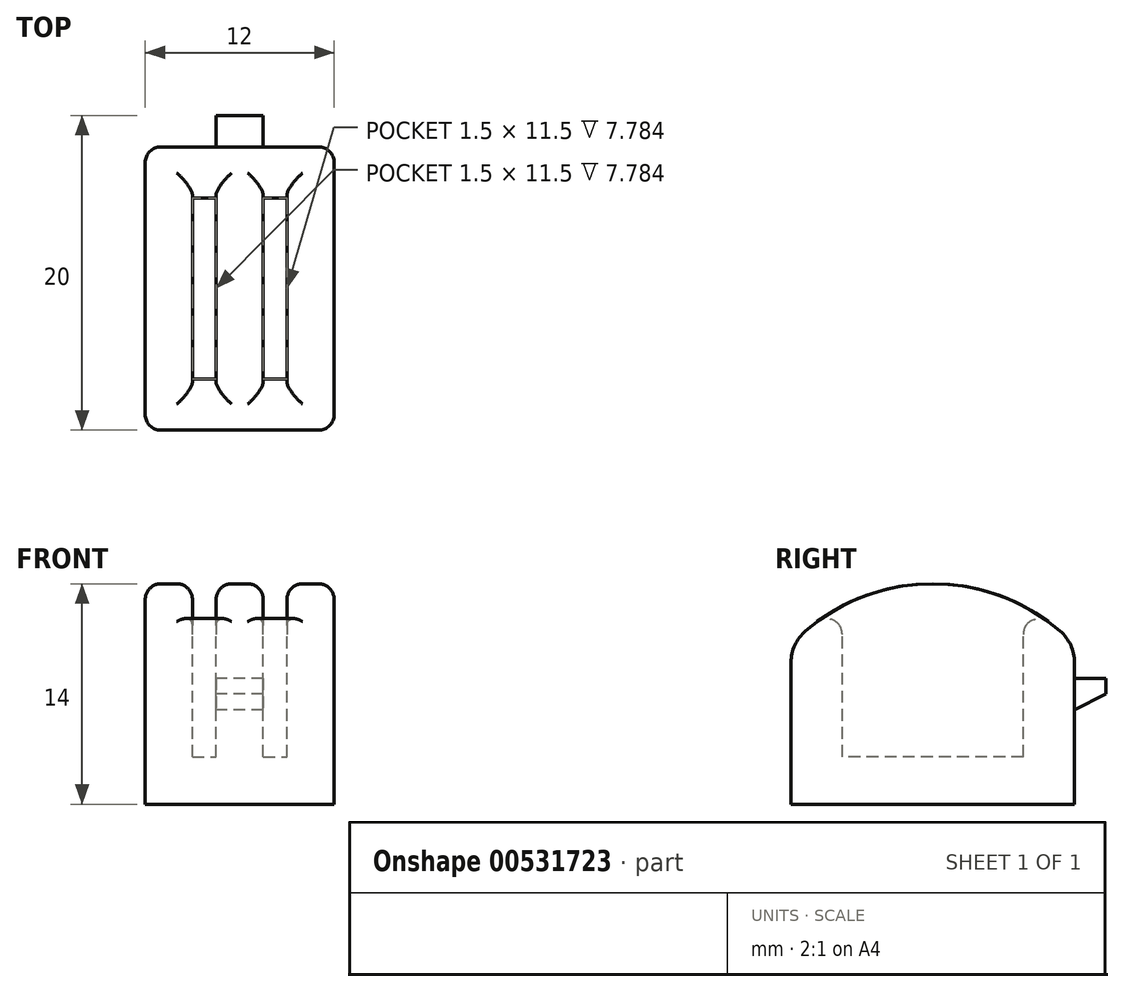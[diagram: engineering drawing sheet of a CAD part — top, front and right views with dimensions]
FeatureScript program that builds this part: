
annotation { "Feature Type Name" : "Feature", "Feature Type Description" : "" }
export const myFeature = defineFeature(function(context is Context, id is Id, definition is map)
    precondition{}
    {
        {
            var Q0;
            Q0=qCreatedBy(makeId("Right.planeOp"),FACE);
            var sketch = newSketch(context, id + "F0", { "sketchPlane" : qUnion([Q0])});
            skLineSegment(sketch, "E0.bottom", {"start": v(-9, 0) * mm, "end": v(9, 0) * mm});
            skLineSegment(sketch, "E0.top", {"start": v(-9, 14) * mm, "end": v(9, 14) * mm, "construction": true});
            skLineSegment(sketch, "E0.left", {"start": v(-9, 0) * mm, "end": v(-9, 14) * mm, "construction": true});
            skLineSegment(sketch, "E0.right", {"start": v(9, 0) * mm, "end": v(9, 14) * mm, "construction": true});
            skLineSegment(sketch, "E1", {"start": v(-9, 11) * mm, "end": v(9, 11) * mm, "construction": true});
            skArc(sketch, "E2", {"start": v(-8.08, 11) * mm, "mid": v(-8.76, 10.1) * mm, "end": v(-9, 9) * mm});
            skArc(sketch, "E3", {"start": v(9, 9) * mm, "mid": v(8.76, 10.1) * mm, "end": v(8.08, 11) * mm});
            skLineSegment(sketch, "E4", {"start": v(-9, 9) * mm, "end": v(9, 9) * mm, "construction": true});
            skArc(sketch, "E5", {"start": v(8.08, 11) * mm, "mid": v(0, 14) * mm, "end": v(-8.08, 11) * mm});
            skLineSegment(sketch, "E6", {"start": v(-9, 0) * mm, "end": v(-9, 9) * mm});
            skLineSegment(sketch, "E7", {"start": v(9, 9) * mm, "end": v(9, 0) * mm});
            skSolve(sketch);
        }
        {
            var Q0;
            Q0=makeQuery(id+"F0.imprint","IMPRINT",FACE,{"disambiguationData":[TD([[makeQuery(id+"F0.imprint","IMPRINT",EDGE,{"derivedFrom":sQuery(id+"F0.wireOp",EDGE,"E0.bottom")}),1.0]])]});
            extrude(context, id + "F1", {"entities" : qUnion([Q0]), "endBound" : BoundingType.SYMMETRIC, "oppositeDirection" : true, "depth" : 12 * mm, "offsetDistance" : 25.4 * mm, "hasSecondDirection" : true, "secondDirectionOppositeDirection" : false, "secondDirectionDepth" : 25.4 * mm});
        }
        {
            var Q0;
            Q0=qCreatedBy(makeId("Top.planeOp"),FACE);
            cPlane(context, id + "F2", {"entities" : qUnion([Q0]), "cplaneType" : CPlaneType.OFFSET, "offset" : 18 * mm, "width" : 152.4 * mm, "height" : 152.4 * mm});
        }
        {
            var Q0;
            Q0=qCreatedBy(id+"F2.planeOp",FACE);
            var sketch = newSketch(context, id + "F3", { "sketchPlane" : qUnion([Q0])});
            skLineSegment(sketch, "E8.bottom", {"start": v(-3, 5.75) * mm, "end": v(-1.5, 5.75) * mm});
            skLineSegment(sketch, "E8.top", {"start": v(-3, -5.75) * mm, "end": v(-1.5, -5.75) * mm});
            skLineSegment(sketch, "E8.left", {"start": v(-3, 5.75) * mm, "end": v(-3, -5.75) * mm});
            skLineSegment(sketch, "E8.right", {"start": v(-1.5, 5.75) * mm, "end": v(-1.5, -5.75) * mm});
            skLineSegment(sketch, "E9.bottom", {"start": v(1.5, 5.75) * mm, "end": v(3, 5.75) * mm});
            skLineSegment(sketch, "E9.top", {"start": v(1.5, -5.75) * mm, "end": v(3, -5.75) * mm});
            skLineSegment(sketch, "E9.left", {"start": v(1.5, 5.75) * mm, "end": v(1.5, -5.75) * mm});
            skLineSegment(sketch, "E9.right", {"start": v(3, 5.75) * mm, "end": v(3, -5.75) * mm});
            skLineSegment(sketch, "E10.0", {"start": v(-6, 9) * mm, "end": v(6, 9) * mm});
            skLineSegment(sketch, "E11.0", {"start": v(6, 8.08) * mm, "end": v(6, -8.08) * mm});
            skLineSegment(sketch, "E12.0", {"start": v(-6, 8.08) * mm, "end": v(-6, -8.08) * mm});
            skLineSegment(sketch, "E13.0", {"start": v(-6, -9) * mm, "end": v(6, -9) * mm});
            skLineSegment(sketch, "E14", {"start": v(-3, -5.75) * mm, "end": v(-6, -5.75) * mm, "construction": true});
            skLineSegment(sketch, "E15", {"start": v(-1.5, -5.75) * mm, "end": v(1.5, -5.75) * mm, "construction": true});
            skLineSegment(sketch, "E16", {"start": v(3, -5.75) * mm, "end": v(6, -5.75) * mm, "construction": true});
            skSolve(sketch);
        }
        {
            var Q0;
            Q0 = qSketchRegion(id + "F3", true);
            extrude(context, id + "F4", {"entities" : qUnion([Q0]), "operationType" : NewBodyOperationType.REMOVE, "oppositeDirection" : true, "depth" : 15 * mm, "offsetDistance" : 25.4 * mm});
        }
        {
            var Q0;
            Q0=qCreatedBy(makeId("Right.planeOp"),FACE);
            var sketch = newSketch(context, id + "F5", { "sketchPlane" : qUnion([Q0])});
            skLineSegment(sketch, "E17.0", {"start": v(9, 9) * mm, "end": v(9, 0) * mm});
            skLineSegment(sketch, "E18", {"start": v(9, 6) * mm, "end": v(11, 7) * mm});
            skLineSegment(sketch, "E19", {"start": v(11, 7) * mm, "end": v(11, 8) * mm});
            skLineSegment(sketch, "E20", {"start": v(11, 8) * mm, "end": v(9, 8) * mm});
            skSolve(sketch);
        }
        {
            var Q0;
            {var subQ0=sQuery(id+"F5.wireOp",EDGE,"E18");Q0=makeQuery(id+"F5.imprint","IMPRINT",FACE,{"disambiguationData":[TD([[makeQuery(id+"F5.imprint","IMPRINT",EDGE,{"derivedFrom":subQ0}),1.0]])]});}
            extrude(context, id + "F6", {"entities" : qUnion([Q0]), "operationType" : NewBodyOperationType.ADD, "endBound" : BoundingType.SYMMETRIC, "depth" : 3 * mm, "offsetDistance" : 25.4 * mm});
        }
        {
            var Q0;
            Q0=makeQuery(id+"F1.opExtrude","CAP_EDGE",EDGE,{"disambiguationData":[OSD([sQuery(id+"F0.wireOp",EDGE,"E6")])],"isStart":true});
            var Q1;
            Q1=makeQuery(id+"F1.opExtrude","CAP_EDGE",EDGE,{"disambiguationData":[OSD([sQuery(id+"F0.wireOp",EDGE,"E6")])],"isStart":false});
            var Q2;
            Q2=makeQuery(id+"F4.boolean.opBoolean","INTERSECT",EDGE,{"derivedFrom":[makeQuery(id+"F1.opExtrude","SWEPT_FACE",FACE,{"disambiguationData":[OSD([sQuery(id+"F0.wireOp",EDGE,"E5")])]}),makeQuery(id+"F4.opExtrude","SWEPT_FACE",FACE,{"disambiguationData":[OSD([sQuery(id+"F3.wireOp",EDGE,"E9.left")])]})]});
            var Q3;
            Q3=makeQuery(id+"F4.boolean.opBoolean","INTERSECT",EDGE,{"derivedFrom":[makeQuery(id+"F1.opExtrude","SWEPT_FACE",FACE,{"disambiguationData":[OSD([sQuery(id+"F0.wireOp",EDGE,"E5")])]}),makeQuery(id+"F4.opExtrude","SWEPT_FACE",FACE,{"disambiguationData":[OSD([sQuery(id+"F3.wireOp",EDGE,"E9.right")])]})]});
            var Q4;
            Q4=makeQuery(id+"F4.boolean.opBoolean","INTERSECT",EDGE,{"derivedFrom":[makeQuery(id+"F1.opExtrude","SWEPT_FACE",FACE,{"disambiguationData":[OSD([sQuery(id+"F0.wireOp",EDGE,"E5")])]}),makeQuery(id+"F4.opExtrude","SWEPT_FACE",FACE,{"disambiguationData":[OSD([sQuery(id+"F3.wireOp",EDGE,"E9.top")])]})]});
            var Q5;
            Q5=makeQuery(id+"F4.boolean.opBoolean","INTERSECT",EDGE,{"derivedFrom":[makeQuery(id+"F1.opExtrude","SWEPT_FACE",FACE,{"disambiguationData":[OSD([sQuery(id+"F0.wireOp",EDGE,"E5")])]}),makeQuery(id+"F4.opExtrude","SWEPT_FACE",FACE,{"disambiguationData":[OSD([sQuery(id+"F3.wireOp",EDGE,"E9.bottom")])]})]});
            var Q6;
            Q6=makeQuery(id+"F4.boolean.opBoolean","INTERSECT",EDGE,{"derivedFrom":[makeQuery(id+"F1.opExtrude","SWEPT_FACE",FACE,{"disambiguationData":[OSD([sQuery(id+"F0.wireOp",EDGE,"E5")])]}),makeQuery(id+"F4.opExtrude","SWEPT_FACE",FACE,{"disambiguationData":[OSD([sQuery(id+"F3.wireOp",EDGE,"E8.right")])]})]});
            var Q7;
            Q7=makeQuery(id+"F4.boolean.opBoolean","INTERSECT",EDGE,{"derivedFrom":[makeQuery(id+"F1.opExtrude","SWEPT_FACE",FACE,{"disambiguationData":[OSD([sQuery(id+"F0.wireOp",EDGE,"E5")])]}),makeQuery(id+"F4.opExtrude","SWEPT_FACE",FACE,{"disambiguationData":[OSD([sQuery(id+"F3.wireOp",EDGE,"E8.top")])]})]});
            var Q8;
            Q8=makeQuery(id+"F4.boolean.opBoolean","INTERSECT",EDGE,{"derivedFrom":[makeQuery(id+"F1.opExtrude","SWEPT_FACE",FACE,{"disambiguationData":[OSD([sQuery(id+"F0.wireOp",EDGE,"E5")])]}),makeQuery(id+"F4.opExtrude","SWEPT_FACE",FACE,{"disambiguationData":[OSD([sQuery(id+"F3.wireOp",EDGE,"E8.left")])]})]});
            var Q9;
            Q9=makeQuery(id+"F4.boolean.opBoolean","INTERSECT",EDGE,{"derivedFrom":[makeQuery(id+"F1.opExtrude","SWEPT_FACE",FACE,{"disambiguationData":[OSD([sQuery(id+"F0.wireOp",EDGE,"E5")])]}),makeQuery(id+"F4.opExtrude","SWEPT_FACE",FACE,{"disambiguationData":[OSD([sQuery(id+"F3.wireOp",EDGE,"E8.bottom")])]})]});
            fillet(context, id + "F7", {"entities" : qUnion([Q0, Q1, Q2, Q3, Q4, Q5, Q6, Q7, Q8, Q9]), "radius" : 1 * mm, "tangentPropagation" : true, "allowEdgeOverflow" : false});
        }
    });
